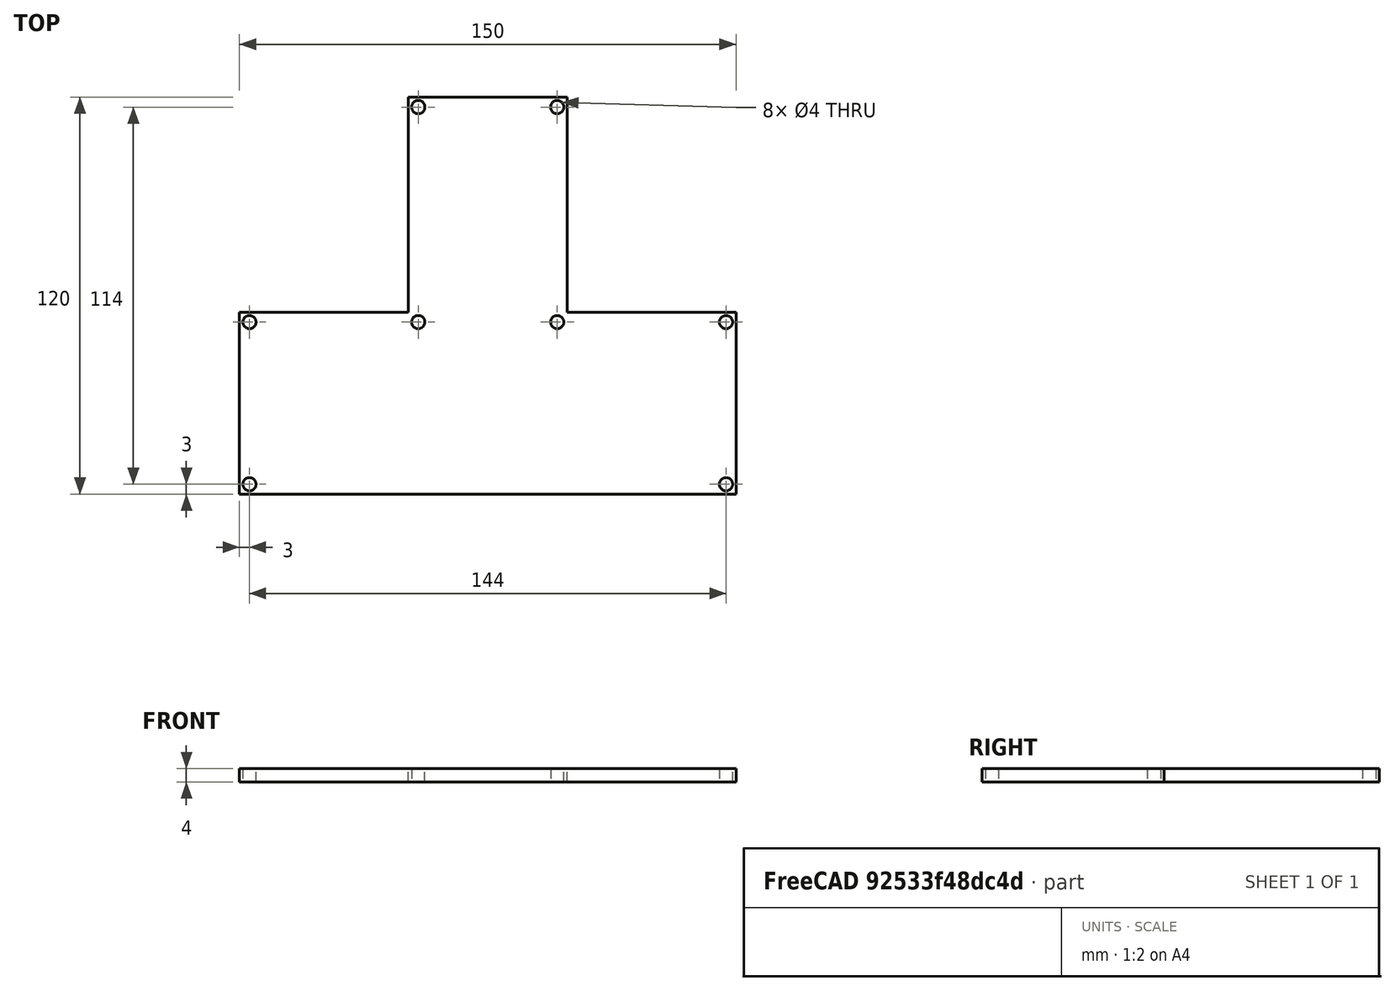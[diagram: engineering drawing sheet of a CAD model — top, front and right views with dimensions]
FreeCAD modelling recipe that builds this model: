
FCSTD DOCUMENT  (FreeCAD 0.19R)
Label: cover
License: All rights reserved
LicenseURL: http://en.wikipedia.org/wiki/All_rights_reserved
objects: Sketcher::SketchObject×1, PartDesign::Pad×1, PartDesign::CoordinateSystem×1, PartDesign::Body×1
note: 5 computed .brp shape members not serialized (recipe doc carries the construction recipe); baked Part::Feature solids carry a one-line shape summary decoded from their .brp

FEATURE [Sketcher::SketchObject] Sketch
  FullyConstrained = true
  MapMode = 5
  Support = -> [XY_Plane]
  sketch-geometry (16):
    g0: LineSegment StartX=-24 StartY=120 StartZ=0 EndX=24 EndY=120 EndZ=0
    g1: LineSegment StartX=24 StartY=120 StartZ=0 EndX=24 EndY=55 EndZ=0
    g2: LineSegment StartX=24 StartY=55 StartZ=0 EndX=75 EndY=55 EndZ=0
    g3: LineSegment StartX=75 StartY=55 StartZ=0 EndX=75 EndY=0 EndZ=0
    g4: LineSegment StartX=75 StartY=0 StartZ=0 EndX=-75 EndY=0 EndZ=0
    g5: LineSegment StartX=-75 StartY=0 StartZ=0 EndX=-75 EndY=55 EndZ=0
    g6: LineSegment StartX=-75 StartY=55 StartZ=0 EndX=-24 EndY=55 EndZ=0
    g7: LineSegment StartX=-24 StartY=55 StartZ=0 EndX=-24 EndY=120 EndZ=0
    g8: Circle CenterX=-21 CenterY=52 CenterZ=0 NormalX=0 NormalY=0 NormalZ=1 AngleXU=0 Radius=2
    g9: Circle CenterX=-21 CenterY=117 CenterZ=0 NormalX=0 NormalY=0 NormalZ=1 AngleXU=0 Radius=2
    g10: Circle CenterX=21 CenterY=117 CenterZ=0 NormalX=0 NormalY=0 NormalZ=1 AngleXU=0 Radius=2
    g11: Circle CenterX=21 CenterY=52 CenterZ=0 NormalX=0 NormalY=0 NormalZ=1 AngleXU=0 Radius=2
    g12: Circle CenterX=72 CenterY=52 CenterZ=0 NormalX=0 NormalY=0 NormalZ=1 AngleXU=0 Radius=2
    g13: Circle CenterX=72 CenterY=3 CenterZ=0 NormalX=0 NormalY=0 NormalZ=1 AngleXU=0 Radius=2
    g14: Circle CenterX=-72 CenterY=52 CenterZ=0 NormalX=0 NormalY=0 NormalZ=1 AngleXU=0 Radius=2
    g15: Circle CenterX=-72 CenterY=3 CenterZ=0 NormalX=0 NormalY=0 NormalZ=1 AngleXU=0 Radius=2
  constraints (46):
    c: Coincident(g0,g1)
    c: Vertical(g1)
    c: Coincident(g1,g2)
    c: Horizontal(g2)
    c: Coincident(g2,g3)
    c: Vertical(g3)
    c: Coincident(g3,g4)
    c: Coincident(g4,g5)
    c: Vertical(g5)
    c: Coincident(g5,g6)
    c: Horizontal(g6)
    c: Coincident(g6,g7)
    c: Coincident(g7,g0)
    c: Vertical(g7)
    c: Horizontal(g6,g1)
    c: Symmetric(g0,g0,g-2)
    c: Symmetric(g4,g3,g-2)
    c: PointOnObject(g4,g-1)
    c: DistanceX(g4,g4) = 150
    c: DistanceY(g3,g0) = 120
    c: DistanceY(g1,g1) = 65
    c: DistanceX(g0,g0) = 48
    c: Equal(g13,g12)
    c: Equal(g12,g11)
    c: Equal(g11,g10)
    c: Equal(g10,g9)
    c: Equal(g9,g8)
    c: Equal(g8,g14)
    c: Equal(g14,g15)
    c: Diameter(g11) = 4
    c: DistanceX(g0,g9) = 3
    c: DistanceY(g9,g0) = 3
    c: Horizontal(g10,g9)
    c: DistanceX(g10,g0) = 3
    c: Vertical(g11,g10)
    c: DistanceY(g11,g1) = 3
    c: Horizontal(g11,g8)
    c: Horizontal(g8,g12)
    c: Horizontal(g12,g14)
    c: Vertical(g9,g8)
    c: DistanceX(g5,g14) = 3
    c: DistanceX(g12,g2) = 3
    c: Vertical(g15,g14)
    c: Vertical(g13,g12)
    c: Horizontal(g13,g15)
    c: DistanceY(g3,g13) = 3
FEATURE [PartDesign::Pad] Pad
  Direction = (1,1,1)
  Length = 4
  Length2 = 100
  Profile = -> Sketch
  Type = 0
FEATURE [PartDesign::CoordinateSystem] LCS_1
  AttacherType = Attacher::AttachEngine3D
  MapMode = 11
  Placement = pos=(-21,117,0) rot=(0,0,1;1.5708rad)
  Support = -> [Pad]
FEATURE [PartDesign::Body] Body
  Group = -> [Sketch,Pad,LCS_1]
  Origin = -> Origin
  Tip = -> Pad
